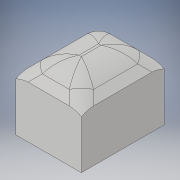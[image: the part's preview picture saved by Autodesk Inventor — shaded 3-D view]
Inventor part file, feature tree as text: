
AUTODESK INVENTOR PART (.ipt)
format: ipt  version: 2019 (Build 230136000, 136)  size: 141,312 bytes
history: native  units: mm
features: fillet x2, other x1, extrude x1, chamfer x1, sketch x1
ambient origin geometry x8: Origin, YZ Plane, XZ Plane, XY Plane, X Axis, Y Axis, Z Axis, Center Point
bodies: Body1 (feature_tree)
feature tree (6):
  other  "Твердое тело1"
  extrude  "Выдавливание1"  Depth=3.8mm
  chamfer  "Фаска1"  Distance=4.0mm
  fillet  "Сопряжение1"  Radius=1.0mm
  fillet  "Сопряжение2"  Radius=2.0mm
  sketch  "Эскиз1"
